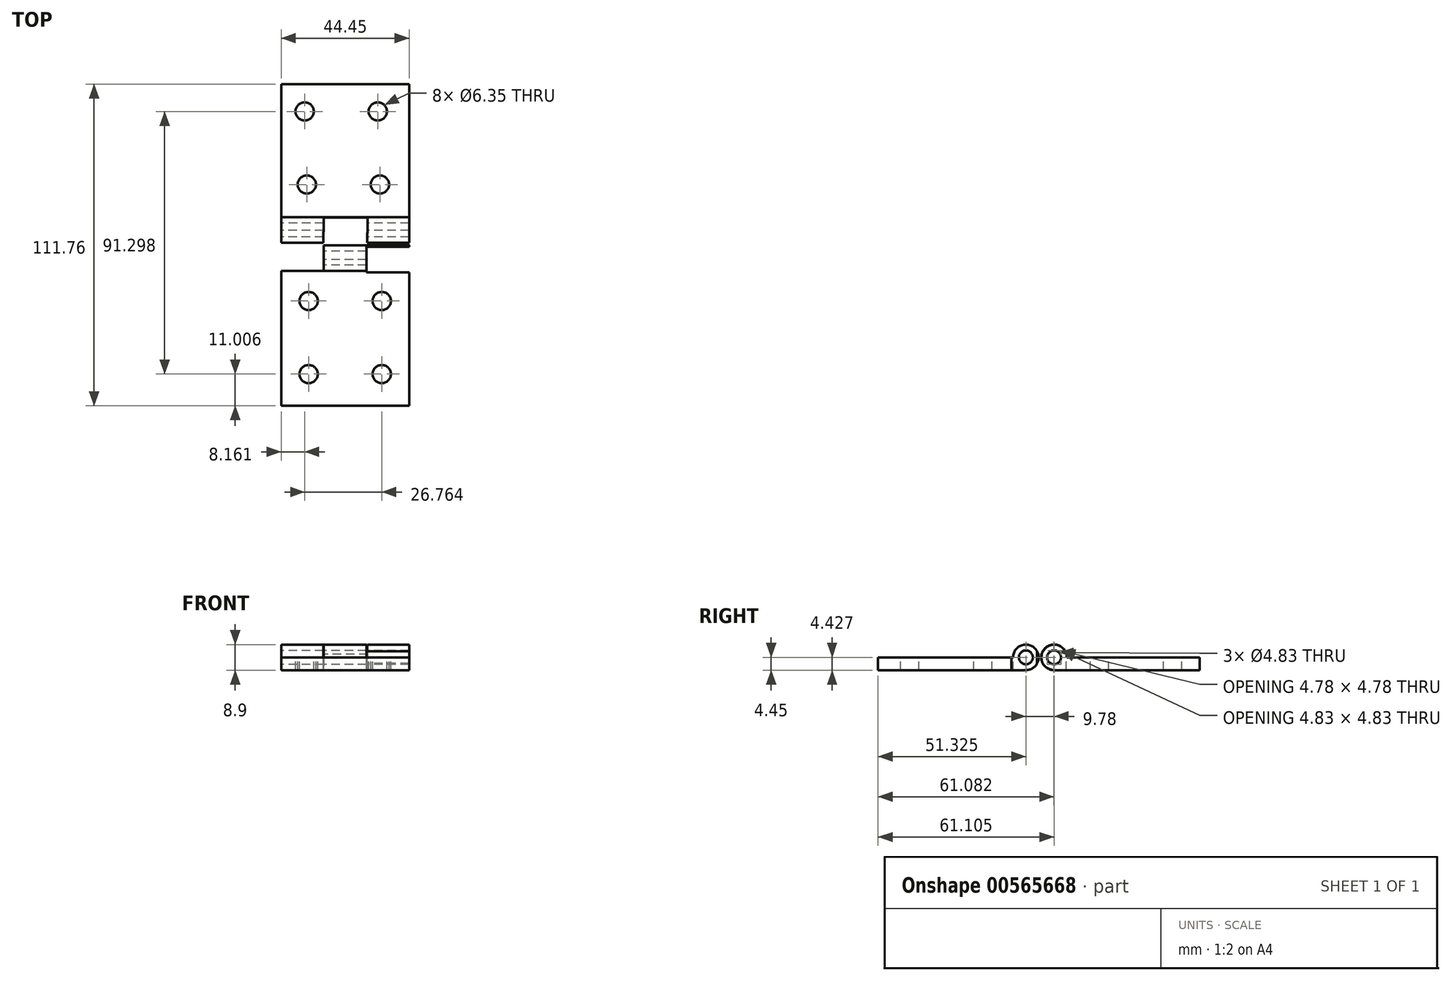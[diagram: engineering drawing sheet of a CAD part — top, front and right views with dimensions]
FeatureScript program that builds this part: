
annotation { "Feature Type Name" : "Feature", "Feature Type Description" : "" }
export const myFeature = defineFeature(function(context is Context, id is Id, definition is map)
    precondition{}
    {
        {
            var Q0;
            Q0=qCreatedBy(makeId("Top.planeOp"),FACE);
            var sketch = newSketch(context, id + "F0", { "sketchPlane" : qUnion([Q0])});
            skLineSegment(sketch, "E0.bottom", {"start": v(0, 5.08) * mm, "end": v(44.45, 5.08) * mm});
            skLineSegment(sketch, "E0.top", {"start": v(0, 55.88) * mm, "end": v(44.45, 55.88) * mm});
            skLineSegment(sketch, "E0.left", {"start": v(0, 5.08) * mm, "end": v(0, 55.88) * mm});
            skLineSegment(sketch, "E0.right", {"start": v(44.45, 5.08) * mm, "end": v(44.45, 55.88) * mm});
            skLineSegment(sketch, "E1.bottom", {"start": v(0, -5.08) * mm, "end": v(44.45, -5.08) * mm});
            skLineSegment(sketch, "E1.top", {"start": v(0, -55.88) * mm, "end": v(44.45, -55.88) * mm});
            skLineSegment(sketch, "E1.left", {"start": v(0, -5.08) * mm, "end": v(0, -55.88) * mm});
            skLineSegment(sketch, "E1.right", {"start": v(44.45, -5.08) * mm, "end": v(44.45, -55.88) * mm});
            skSolve(sketch);
        }
        {
            var Q0;
            Q0=qCreatedBy(makeId("Right.planeOp"),FACE);
            var sketch = newSketch(context, id + "F1", { "sketchPlane" : qUnion([Q0])});
            skCircle(sketch, "E2", {"center": v(5.22, 0) * mm, "radius": 4.45 * mm});
            skCircle(sketch, "E3", {"center": v(-4.56, 0) * mm, "radius": 4.45 * mm});
            skSolve(sketch);
        }
        {
            var Q0;
            Q0=makeQuery(id+"F0.imprint","IMPRINT",FACE,{"disambiguationData":[TD([[makeQuery(id+"F0.imprint","IMPRINT",EDGE,{"derivedFrom":sQuery(id+"F0.wireOp",EDGE,"E0.bottom")}),1.0]])]});
            extrude(context, id + "F2", {"entities" : qUnion([Q0]), "oppositeDirection" : true, "depth" : 4.44 * mm});
        }
        {
            var Q0;
            Q0=makeQuery(id+"F0.imprint","IMPRINT",FACE,{"disambiguationData":[TD([[makeQuery(id+"F0.imprint","IMPRINT",EDGE,{"derivedFrom":sQuery(id+"F0.wireOp",EDGE,"E1.bottom")}),-1.0]])]});
            extrude(context, id + "F3", {"entities" : qUnion([Q0]), "oppositeDirection" : true, "depth" : 4.44 * mm});
        }
        {
            var Q0;
            Q0=makeQuery(id+"F1.imprint","IMPRINT",FACE,{"disambiguationData":[TD([[makeQuery(id+"F1.imprint","IMPRINT",EDGE,{"derivedFrom":sQuery(id+"F1.wireOp",EDGE,"E2")}),1.0]])]});
            var Q1;
            Q1=makeQuery(id+"F1.imprint","IMPRINT",FACE,{"disambiguationData":[TD([[makeQuery(id+"F1.imprint","IMPRINT",EDGE,{"derivedFrom":sQuery(id+"F1.wireOp",EDGE,"E3")}),1.0]])]});
            extrude(context, id + "F4", {"entities" : qUnion([Q0, Q1]), "depth" : 44.45 * mm});
        }
        {
            var Q0;
            Q0=makeQuery(id+"F4.opExtrude","SWEPT_BODY",BODY,{"disambiguationData":[OSD([sQuery(id+"F1.wireOp",EDGE,"E2")])]});
            var Q1;
            Q1=makeQuery(id+"F2.opExtrude","SWEPT_BODY",BODY,{"disambiguationData":[OSD([sQuery(id+"F0.wireOp",EDGE,"E0.bottom"),sQuery(id+"F0.wireOp",EDGE,"E0.top"),sQuery(id+"F0.wireOp",EDGE,"E0.left"),sQuery(id+"F0.wireOp",EDGE,"E0.right")])]});
            var Q2;
            Q2=makeQuery(id+"F4.opExtrude","SWEPT_BODY",BODY,{"disambiguationData":[OSD([sQuery(id+"F1.wireOp",EDGE,"E3")])]});
            var Q3;
            Q3=makeQuery(id+"F3.opExtrude","SWEPT_BODY",BODY,{"disambiguationData":[OSD([sQuery(id+"F0.wireOp",EDGE,"E1.bottom"),sQuery(id+"F0.wireOp",EDGE,"E1.top"),sQuery(id+"F0.wireOp",EDGE,"E1.left"),sQuery(id+"F0.wireOp",EDGE,"E1.right")])]});
            booleanBodies(context, id + "F5", {"operationType" : BooleanOperationType.UNION, "tools" : qUnion([Q0, Q1, Q2, Q3])});
        }
        {
            var Q0;
            Q0=qCreatedBy(makeId("Top.planeOp"),FACE);
            var sketch = newSketch(context, id + "F6", { "sketchPlane" : qUnion([Q0])});
            skLineSegment(sketch, "E4.bottom", {"start": v(0, -0.11) * mm, "end": v(14.8, -0.11) * mm});
            skLineSegment(sketch, "E4.top", {"start": v(0, -9) * mm, "end": v(14.8, -9) * mm});
            skLineSegment(sketch, "E4.left", {"start": v(0, -0.11) * mm, "end": v(0, -9) * mm});
            skLineSegment(sketch, "E4.right", {"start": v(14.8, -0.11) * mm, "end": v(14.8, -9) * mm});
            skLineSegment(sketch, "E5.bottom", {"start": v(14.8, 9.53) * mm, "end": v(30.05, 9.53) * mm});
            skLineSegment(sketch, "E5.top", {"start": v(14.63, 0.64) * mm, "end": v(29.87, 0.64) * mm});
            skLineSegment(sketch, "E5.left", {"start": v(14.8, 9.53) * mm, "end": v(14.63, 0.64) * mm});
            skLineSegment(sketch, "E5.right", {"start": v(30.05, 9.53) * mm, "end": v(29.87, 0.64) * mm});
            skPoint(sketch, "E6.firstSnap0", {"position": v(29.96, 5.08) * mm});
            skLineSegment(sketch, "E6.bottom", {"start": v(29.62, -0.64) * mm, "end": v(44.48, -0.64) * mm});
            skLineSegment(sketch, "E6.top", {"start": v(29.62, -9.53) * mm, "end": v(44.48, -9.53) * mm});
            skLineSegment(sketch, "E6.left", {"start": v(29.62, -0.64) * mm, "end": v(29.62, -9.53) * mm});
            skLineSegment(sketch, "E6.right", {"start": v(44.48, -0.64) * mm, "end": v(44.48, -9.53) * mm});
            skSolve(sketch);
        }
        {
            var Q0;
            Q0=makeQuery(id+"F6.imprint","IMPRINT",FACE,{"disambiguationData":[TD([[makeQuery(id+"F6.imprint","IMPRINT",EDGE,{"derivedFrom":sQuery(id+"F6.wireOp",EDGE,"E4.bottom")}),-1.0]])]});
            var Q1;
            Q1=makeQuery(id+"F6.imprint","IMPRINT",FACE,{"disambiguationData":[TD([[makeQuery(id+"F6.imprint","IMPRINT",EDGE,{"derivedFrom":sQuery(id+"F6.wireOp",EDGE,"E6.bottom")}),-1.0]])]});
            extrude(context, id + "F7", {"entities" : qUnion([Q0, Q1]), "operationType" : NewBodyOperationType.REMOVE, "oppositeDirection" : true, "depth" : 5.08 * mm, "hasSecondDirection" : true, "secondDirectionOppositeDirection" : false, "secondDirectionDepth" : 5.08 * mm});
        }
        {
            var Q0;
            Q0=makeQuery(id+"F6.imprint","IMPRINT",FACE,{"disambiguationData":[TD([[makeQuery(id+"F6.imprint","IMPRINT",EDGE,{"derivedFrom":sQuery(id+"F6.wireOp",EDGE,"E5.bottom")}),-1.0]])]});
            extrude(context, id + "F8", {"entities" : qUnion([Q0]), "operationType" : NewBodyOperationType.REMOVE, "oppositeDirection" : true, "depth" : 5.08 * mm, "hasSecondDirection" : true, "secondDirectionOppositeDirection" : false, "secondDirectionDepth" : 5.08 * mm});
        }
        {
            var Q0;
            Q0=makeQuery(id+"F1.imprint","IMPRINT",FACE,{"disambiguationData":[TD([[makeQuery(id+"F1.imprint","IMPRINT",EDGE,{"derivedFrom":sQuery(id+"F1.wireOp",EDGE,"E2")}),1.0]])]});
            var sketch = newSketch(context, id + "F9", { "sketchPlane" : qUnion([Q0])});
            skCircle(sketch, "E7", {"center": v(-4.56, 0) * mm, "radius": 2.41 * mm});
            skSolve(sketch);
        }
        {
            var Q0;
            Q0=makeQuery(id+"F9.imprint","IMPRINT",FACE,{"disambiguationData":[TD([[makeQuery(id+"F9.imprint","IMPRINT",EDGE,{"derivedFrom":sQuery(id+"F9.wireOp",EDGE,"E7")}),1.0]])]});
            extrude(context, id + "F10", {"entities" : qUnion([Q0]), "operationType" : NewBodyOperationType.REMOVE, "endBound" : BoundingType.THROUGH_ALL, "depth" : 25.4 * mm});
        }
        {
            var Q0;
            Q0=makeQuery(id+"F1.imprint","IMPRINT",FACE,{"disambiguationData":[TD([[makeQuery(id+"F1.imprint","IMPRINT",EDGE,{"derivedFrom":sQuery(id+"F1.wireOp",EDGE,"E2")}),1.0]])]});
            var sketch = newSketch(context, id + "F11", { "sketchPlane" : qUnion([Q0])});
            skCircle(sketch, "E8", {"center": v(5.22, 0) * mm, "radius": 2.41 * mm});
            skSolve(sketch);
        }
        {
            var Q0;
            Q0=makeQuery(id+"F11.imprint","IMPRINT",FACE,{"disambiguationData":[TD([[makeQuery(id+"F11.imprint","IMPRINT",EDGE,{"derivedFrom":sQuery(id+"F11.wireOp",EDGE,"E8")}),1.0]])]});
            extrude(context, id + "F12", {"entities" : qUnion([Q0]), "operationType" : NewBodyOperationType.REMOVE, "endBound" : BoundingType.THROUGH_ALL, "depth" : 25.4 * mm});
        }
        {
            var Q0;
            Q0=makeQuery(id+"F2.opExtrude","CAP_FACE",FACE,{"disambiguationData":[OSD([sQuery(id+"F0.wireOp",EDGE,"E0.bottom"),sQuery(id+"F0.wireOp",EDGE,"E0.top"),sQuery(id+"F0.wireOp",EDGE,"E0.left"),sQuery(id+"F0.wireOp",EDGE,"E0.right")])],"isStart":true});
            var sketch = newSketch(context, id + "F13", { "sketchPlane" : qUnion([Q0])});
            skCircle(sketch, "E9", {"center": v(8.89, 21.02) * mm, "radius": 3.18 * mm});
            skCircle(sketch, "E10.1.0.0", {"center": v(34.29, 21.02) * mm, "radius": 3.18 * mm});
            skLineSegment(sketch, "E10.direction1", {"start": v(8.89, 21.02) * mm, "end": v(34.29, 21.02) * mm, "construction": true});
            skCircle(sketch, "E11", {"center": v(8.16, 46.42) * mm, "radius": 3.18 * mm});
            skCircle(sketch, "E12", {"center": v(33.56, 46.42) * mm, "radius": 3.18 * mm});
            skSolve(sketch);
        }
        {
            var Q0;
            Q0=makeQuery(id+"F13.imprint","IMPRINT",FACE,{"disambiguationData":[TD([[makeQuery(id+"F13.imprint","IMPRINT",EDGE,{"derivedFrom":sQuery(id+"F13.wireOp",EDGE,"E9")}),1.0]])]});
            var Q1;
            Q1=makeQuery(id+"F13.imprint","IMPRINT",FACE,{"disambiguationData":[TD([[makeQuery(id+"F13.imprint","IMPRINT",EDGE,{"derivedFrom":sQuery(id+"F13.wireOp",EDGE,"E10.1.0.0")}),1.0]])]});
            extrude(context, id + "F14", {"entities" : qUnion([Q0, Q1]), "operationType" : NewBodyOperationType.REMOVE, "endBound" : BoundingType.THROUGH_ALL, "oppositeDirection" : true, "depth" : 7.62 * mm, "hasSecondDirection" : true, "secondDirectionBound" : SecondDirectionBoundingType.THROUGH_ALL, "secondDirectionOppositeDirection" : false, "secondDirectionDepth" : 25.4 * mm});
        }
        {
            var Q0;
            Q0=makeQuery(id+"F3.opExtrude","CAP_FACE",FACE,{"disambiguationData":[OSD([sQuery(id+"F0.wireOp",EDGE,"E1.bottom"),sQuery(id+"F0.wireOp",EDGE,"E1.top"),sQuery(id+"F0.wireOp",EDGE,"E1.left"),sQuery(id+"F0.wireOp",EDGE,"E1.right")])],"isStart":true});
            var sketch = newSketch(context, id + "F15", { "sketchPlane" : qUnion([Q0])});
            skCircle(sketch, "E13", {"center": v(9.52, -19.47) * mm, "radius": 3.18 * mm});
            skCircle(sketch, "E14.1.0.0", {"center": v(34.92, -19.47) * mm, "radius": 3.18 * mm});
            skLineSegment(sketch, "E14.direction1", {"start": v(9.52, -19.47) * mm, "end": v(34.92, -19.47) * mm, "construction": true});
            skCircle(sketch, "E15", {"center": v(9.52, -44.87) * mm, "radius": 3.18 * mm});
            skCircle(sketch, "E16", {"center": v(34.92, -44.87) * mm, "radius": 3.18 * mm});
            skSolve(sketch);
        }
        {
            var Q0;
            Q0=makeQuery(id+"F15.imprint","IMPRINT",FACE,{"disambiguationData":[TD([[makeQuery(id+"F15.imprint","IMPRINT",EDGE,{"derivedFrom":sQuery(id+"F15.wireOp",EDGE,"E14.1.0.0")}),1.0]])]});
            var Q1;
            Q1=makeQuery(id+"F15.imprint","IMPRINT",FACE,{"disambiguationData":[TD([[makeQuery(id+"F15.imprint","IMPRINT",EDGE,{"derivedFrom":sQuery(id+"F15.wireOp",EDGE,"E13")}),1.0]])]});
            extrude(context, id + "F16", {"entities" : qUnion([Q0, Q1]), "operationType" : NewBodyOperationType.REMOVE, "endBound" : BoundingType.THROUGH_ALL, "oppositeDirection" : true, "depth" : 25.4 * mm});
        }
        {
            var Q0;
            Q0=makeQuery(id+"F0.imprint","IMPRINT",FACE,{"disambiguationData":[TD([[makeQuery(id+"F0.imprint","IMPRINT",EDGE,{"derivedFrom":sQuery(id+"F0.wireOp",EDGE,"E0.bottom")}),1.0]])]});
            var sketch = newSketch(context, id + "F17", { "sketchPlane" : qUnion([Q0])});
            skCircle(sketch, "E17", {"center": v(-91.85, 132.74) * mm, "radius": 25.18 * mm});
            skCircle(sketch, "E18", {"center": v(128.1, 132.74) * mm, "radius": 28.4 * mm});
            skCircle(sketch, "E19", {"center": v(128.1, -63.99) * mm, "radius": 31.75 * mm});
            skSolve(sketch);
        }
        {
            var Q0;
            Q0=sQuery(id+"F17.wireOp",VERTEX,"E17.center");
            var Q1;
            Q1=sQuery(id+"F17.wireOp",VERTEX,"E18.center");
            var Q2;
            Q2=sQuery(id+"F17.wireOp",VERTEX,"E19.center");
            var Q3;
            Q3=makeQuery(id+"F4.opExtrude","SWEPT_BODY",BODY,{"disambiguationData":[OSD([sQuery(id+"F1.wireOp",EDGE,"E2")])]});
            hole(context, id + "F18", {"style" : HoleStyle.SIMPLE, "endStyle" : HoleEndStyle.THROUGH, "holeDiameter" : 6.35 * mm, "isTappedThrough" : true, "tappedDepth" : 12.7 * mm, "tapClearance" : 3, "locations" : qUnion([Q0, Q1, Q2]), "scope" : qUnion([Q3])});
        }
        {
            var Q0;
            Q0=sQuery(id+"F15.wireOp",VERTEX,"E15.center");
            var Q1;
            Q1=sQuery(id+"F15.wireOp",VERTEX,"E16.center");
            var Q2;
            Q2=makeQuery(id+"F4.opExtrude","SWEPT_BODY",BODY,{"disambiguationData":[OSD([sQuery(id+"F1.wireOp",EDGE,"E3")])]});
            hole(context, id + "F19", {"style" : HoleStyle.SIMPLE, "endStyle" : HoleEndStyle.THROUGH, "holeDiameter" : 6.35 * mm, "isTappedThrough" : true, "tappedDepth" : 12.7 * mm, "tapClearance" : 3, "locations" : qUnion([Q0, Q1]), "scope" : qUnion([Q2])});
        }
        {
            var Q0;
            Q0=sQuery(id+"F13.wireOp",VERTEX,"E11.center");
            var Q1;
            Q1=sQuery(id+"F13.wireOp",VERTEX,"E12.center");
            var Q2;
            Q2=makeQuery(id+"F4.opExtrude","SWEPT_BODY",BODY,{"disambiguationData":[OSD([sQuery(id+"F1.wireOp",EDGE,"E2")])]});
            hole(context, id + "F20", {"style" : HoleStyle.SIMPLE, "endStyle" : HoleEndStyle.THROUGH, "holeDiameter" : 6.35 * mm, "isTappedThrough" : true, "tappedDepth" : 12.7 * mm, "tapClearance" : 3, "locations" : qUnion([Q0, Q1]), "scope" : qUnion([Q2])});
        }
    });
